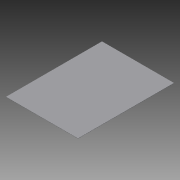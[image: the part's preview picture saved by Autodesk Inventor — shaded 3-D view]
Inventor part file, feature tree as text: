
AUTODESK INVENTOR PART (.ipt)
format: ipt  version: 2015 SP1 (Build 190203100, 203)  size: 69,632 bytes
history: native  units: mm
features: extrude x1, sketch x1
ambient origin geometry x8: Origin, YZ Plane, XZ Plane, XY Plane, X Axis, Y Axis, Z Axis, Center Point
bodies: Solid1 (feature_tree)
feature tree (2):
  extrude  "Extrusion1"  Depth=4000.0mm
  sketch  "Sketch1"  dims[d0=3000.0mm d1=4000.0mm d2=10.0mm d3=0.0mm]
